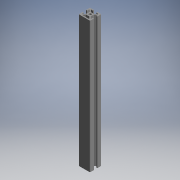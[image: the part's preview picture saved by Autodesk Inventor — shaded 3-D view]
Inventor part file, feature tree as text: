
AUTODESK INVENTOR PART (.ipt)
format: ipt  version: 2017.3 (Build 213256000, 256)  size: 202,240 bytes
history: native  units: mm (DEFAULTED — no unit token found)
features: other x7, sketch x2, extrude x1, hole x1
ambient origin geometry x8: Origin, YZ Plane, XZ Plane, XY Plane, X Axis, Y Axis, Z Axis, Center Point
bodies: Solid1 (feature_tree)
feature tree (11):
  extrude  "Extrusion1"  TaperAngle=0.0deg  [1 undecoded]
  hole  "Hole1"  [1 undecoded]
  other  "C1_XY"
  other  "C1_YZ"
  other  "C1_ZX"
  other  "C1_X"
  other  "C1_Y"
  other  "C1_Z"
  other  "C1_Center"
  sketch  "Sketch_76"  dims[d2=4.2mm d3=6.0mm d4=4.0mm d5=2.0mm d6=90.0deg d7=231.0mm d8=0.0mm d9=0.0mm]
  sketch  "Sketch2"  dims[d0=231.0mm d1=0.0mm]
note: 2 required parameter values undecoded (feature->parameter linkage not recoverable at this tier; creation-order binding heuristic only, values carry confidence <= 0.55)
